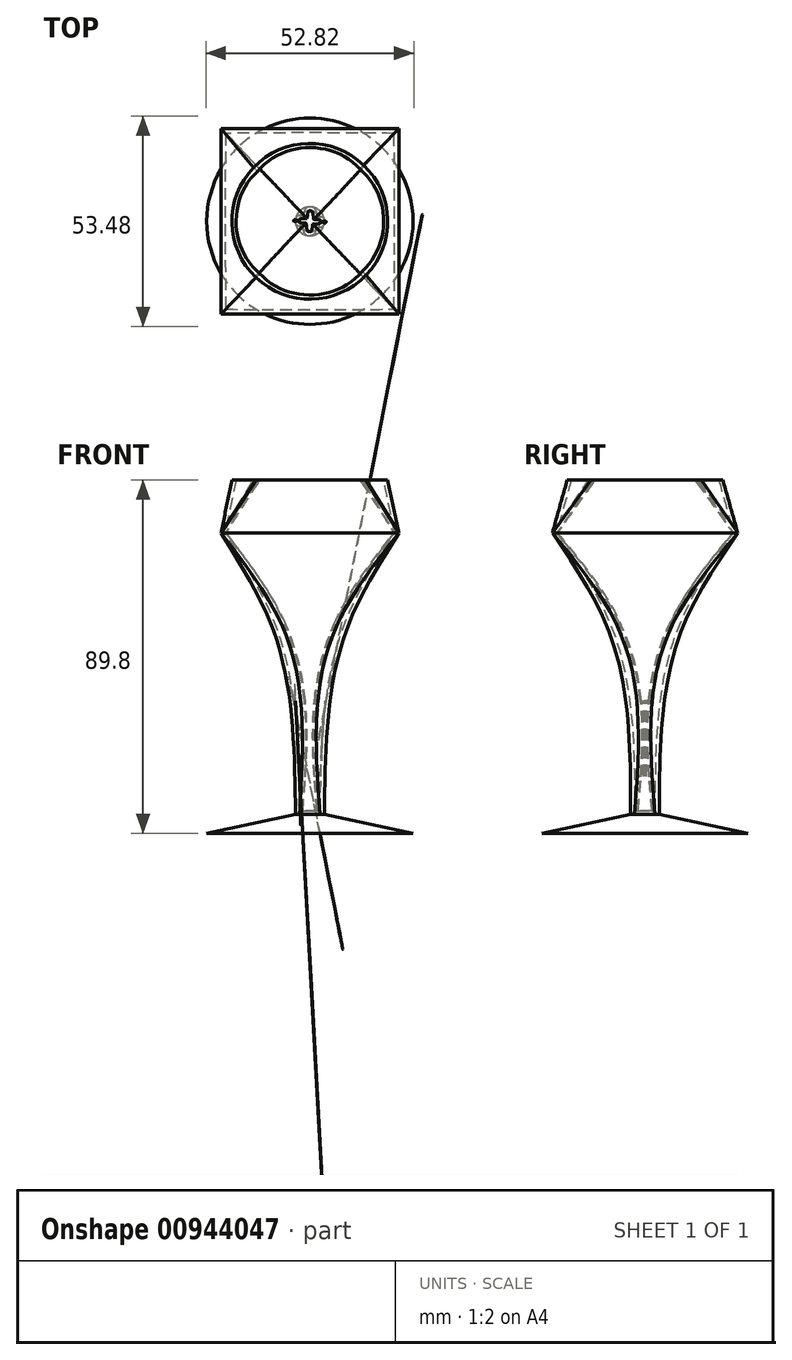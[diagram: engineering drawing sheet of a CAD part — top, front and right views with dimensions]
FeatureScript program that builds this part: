
annotation { "Feature Type Name" : "Feature", "Feature Type Description" : "" }
export const myFeature = defineFeature(function(context is Context, id is Id, definition is map)
    precondition{}
    {
        {
            var Q0;
            Q0=qCreatedBy(makeId("Top.planeOp"),FACE);
            var sketch = newSketch(context, id + "F0", { "sketchPlane" : qUnion([Q0])});
            skCircle(sketch, "E0", {"center": v(0, 0) * mm, "radius": 3.67 * mm});
            skSolve(sketch);
        }
        {
            var Q0;
            Q0=qCreatedBy(makeId("Top.planeOp"),FACE);
            cPlane(context, id + "F1", {"entities" : qUnion([Q0]), "cplaneType" : CPlaneType.OFFSET, "offset" : 85 * mm, "width" : 152.4 * mm, "height" : 152.4 * mm});
        }
        {
            var Q0;
            Q0=qCreatedBy(id+"F1.planeOp",FACE);
            var sketch = newSketch(context, id + "F2", { "sketchPlane" : qUnion([Q0])});
            skCircle(sketch, "E1", {"center": v(0, 0) * mm, "radius": 19.78 * mm});
            skSolve(sketch);
        }
        {
            var Q0;
            Q0=qCreatedBy(makeId("Top.planeOp"),FACE);
            cPlane(context, id + "F3", {"entities" : qUnion([Q0]), "cplaneType" : CPlaneType.OFFSET, "offset" : 47.7 * mm, "width" : 150 * mm, "height" : 150 * mm});
        }
        {
            var Q0;
            Q0=qCreatedBy(makeId("Top.planeOp"),FACE);
            cPlane(context, id + "F4", {"entities" : qUnion([Q0]), "cplaneType" : CPlaneType.OFFSET, "offset" : 71.5 * mm, "width" : 150 * mm, "height" : 150 * mm});
        }
        {
            var Q0;
            Q0=qCreatedBy(id+"F3.planeOp",FACE);
            var sketch = newSketch(context, id + "F5", { "sketchPlane" : qUnion([Q0])});
            skCircle(sketch, "E2", {"center": v(0, 0) * mm, "radius": 9.62 * mm});
            skSolve(sketch);
        }
        {
            var Q0;
            Q0=qCreatedBy(id+"F4.planeOp",FACE);
            var sketch = newSketch(context, id + "F6", { "sketchPlane" : qUnion([Q0])});
            skLineSegment(sketch, "E3.bottom", {"start": v(-22.6, 23.57) * mm, "end": v(22.6, 23.57) * mm});
            skLineSegment(sketch, "E3.top", {"start": v(-22.6, -23.57) * mm, "end": v(22.6, -23.57) * mm});
            skLineSegment(sketch, "E3.left", {"start": v(-22.6, 23.57) * mm, "end": v(-22.6, -23.57) * mm});
            skLineSegment(sketch, "E3.right", {"start": v(22.6, 23.57) * mm, "end": v(22.6, -23.57) * mm});
            skPoint(sketch, "E3.middle", {"position": v(0, 0) * mm});
            skSolve(sketch);
        }
        {
            var Q0;
            Q0=qCreatedBy(makeId("Top.planeOp"),FACE);
            cPlane(context, id + "F7", {"entities" : qUnion([Q0]), "cplaneType" : CPlaneType.OFFSET, "offset" : 4.8 * mm, "oppositeDirection" : true, "width" : 150 * mm, "height" : 150 * mm});
        }
        {
            var Q0;
            Q0=makeQuery(id+"F0.imprint","IMPRINT",FACE,{"disambiguationData":[TD([[makeQuery(id+"F0.imprint","IMPRINT",EDGE,{"derivedFrom":sQuery(id+"F0.wireOp",EDGE,"E0")}),1.0]])]});
            var Q1;
            Q1=makeQuery(id+"F5.imprint","IMPRINT",FACE,{"disambiguationData":[TD([[makeQuery(id+"F5.imprint","IMPRINT",EDGE,{"derivedFrom":sQuery(id+"F5.wireOp",EDGE,"E2")}),1.0]])]});
            var Q2;
            Q2=makeQuery(id+"F6.imprint","IMPRINT",FACE,{"disambiguationData":[TD([[makeQuery(id+"F6.imprint","IMPRINT",EDGE,{"derivedFrom":sQuery(id+"F6.wireOp",EDGE,"E3.bottom")}),-1.0]])]});
            loft(context, id + "F8", {"sheetProfilesArray" : [{ "sheetProfileEntities" : qUnion([Q0]) }, { "sheetProfileEntities" : qUnion([Q1]) }, { "sheetProfileEntities" : qUnion([Q2]) }]});
        }
        {
            var Q0;
            Q0=qCreatedBy(id+"F7.planeOp",FACE);
            var sketch = newSketch(context, id + "F9", { "sketchPlane" : qUnion([Q0])});
            skCircle(sketch, "E4", {"center": v(0, 0) * mm, "radius": 26.2 * mm});
            skSolve(sketch);
        }
        {
            var Q1;
            Q1=makeQuery(id+"F8.opLoft","CAP_FACE",FACE,{"disambiguationData":[OSD([makeQuery(id+"F6.imprint","IMPRINT",FACE,{"disambiguationData":[TD([[makeQuery(id+"F6.imprint","IMPRINT",EDGE,{"derivedFrom":sQuery(id+"F6.wireOp",EDGE,"E3.bottom")}),-1.0]])]})])],"isStart":true});
            var Q2;
            Q2=makeQuery(id+"F2.imprint","IMPRINT",FACE,{"disambiguationData":[TD([[makeQuery(id+"F2.imprint","IMPRINT",EDGE,{"derivedFrom":sQuery(id+"F2.wireOp",EDGE,"E1")}),1.0]])]});
            loft(context, id + "F10", {"operationType" : NewBodyOperationType.ADD, "sheetProfilesArray" : [{ "sheetProfileEntities" : qUnion([Q1]) }, { "sheetProfileEntities" : qUnion([Q2]) }]});
        }
        {
            var Q0;
            Q0=makeQuery(id+"F10.opLoft","CAP_FACE",FACE,{"disambiguationData":[OSD([makeQuery(id+"F2.imprint","IMPRINT",FACE,{"disambiguationData":[TD([[makeQuery(id+"F2.imprint","IMPRINT",EDGE,{"derivedFrom":sQuery(id+"F2.wireOp",EDGE,"E1")}),1.0]])]})])],"isStart":true});
            shell(context, id + "F11", {"entities" : qUnion([Q0]), "thickness" : 1 * mm});
        }
        {
            var Q1;
            Q1=makeQuery(id+"F8.opLoft","CAP_FACE",FACE,{"disambiguationData":[OSD([makeQuery(id+"F0.imprint","IMPRINT",FACE,{"disambiguationData":[TD([[makeQuery(id+"F0.imprint","IMPRINT",EDGE,{"derivedFrom":sQuery(id+"F0.wireOp",EDGE,"E0")}),1.0]])]})])],"isStart":true});
            var Q2;
            Q2=makeQuery(id+"F9.imprint","IMPRINT",FACE,{"disambiguationData":[TD([[makeQuery(id+"F9.imprint","IMPRINT",EDGE,{"derivedFrom":sQuery(id+"F9.wireOp",EDGE,"E4")}),1.0]])]});
            loft(context, id + "F12", {"operationType" : NewBodyOperationType.ADD, "sheetProfilesArray" : [{ "sheetProfileEntities" : qUnion([Q1]) }, { "sheetProfileEntities" : qUnion([Q2]) }]});
        }
    });
